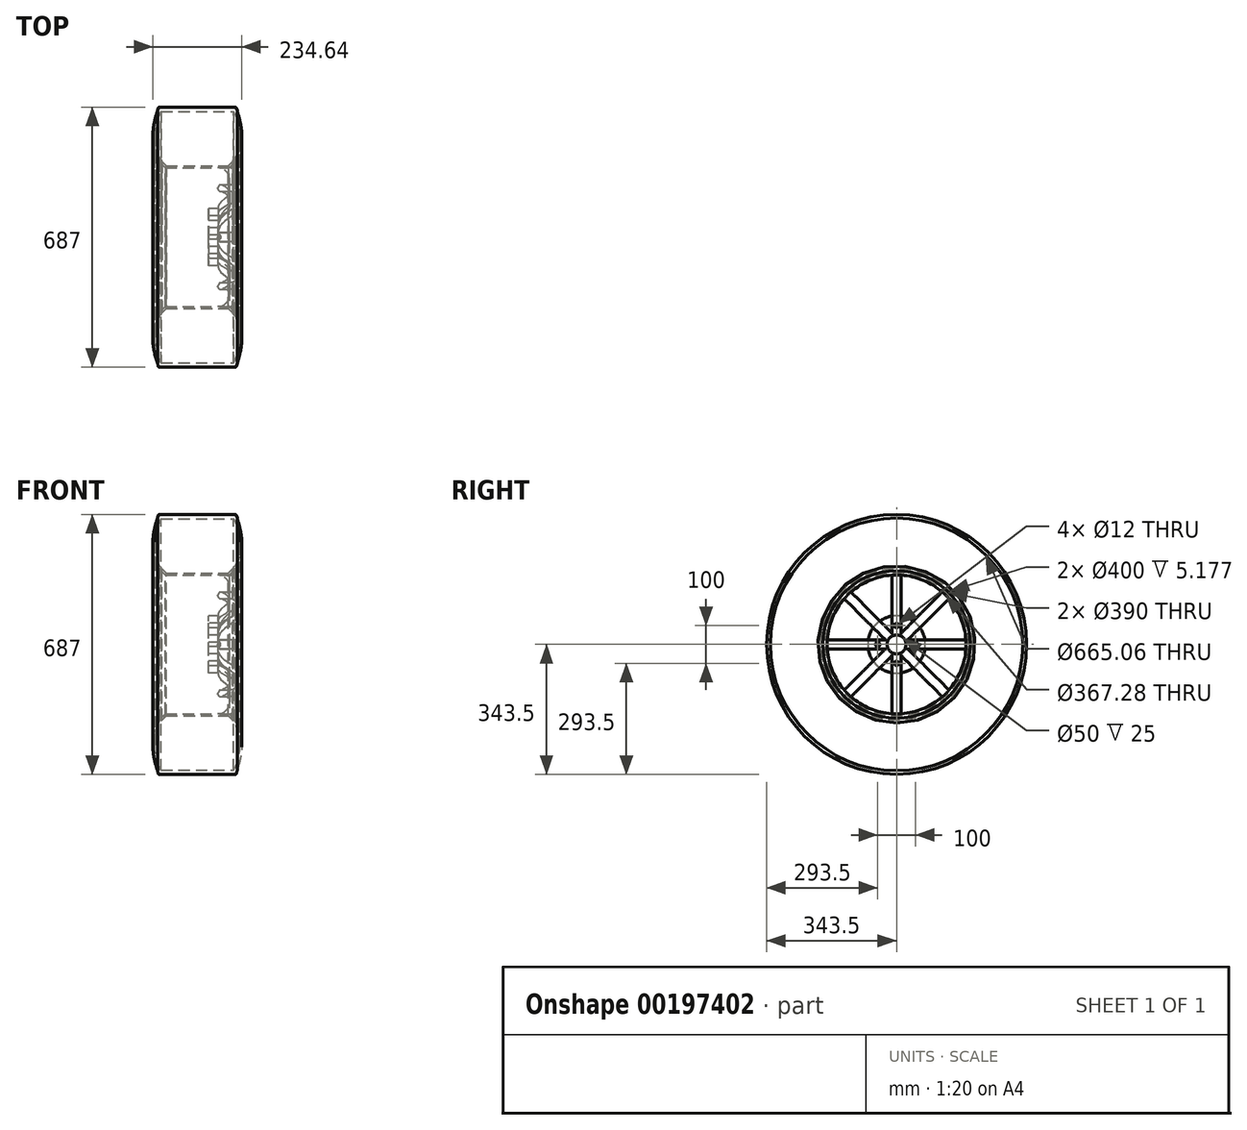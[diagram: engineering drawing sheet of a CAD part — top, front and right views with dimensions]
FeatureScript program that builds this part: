
annotation { "Feature Type Name" : "Feature", "Feature Type Description" : "" }
export const myFeature = defineFeature(function(context is Context, id is Id, definition is map)
    precondition{}
    {
        {
            var Q0;
            Q0=qCreatedBy(makeId("Front.planeOp"),FACE);
            var sketch = newSketch(context, id + "F0", { "sketchPlane" : qUnion([Q0])});
            skLineSegment(sketch, "E0", {"start": v(-136.6, 197.98) * mm, "end": v(-136.6, 205) * mm});
            skLineSegment(sketch, "E1", {"start": v(-131.6, 205) * mm, "end": v(-131.6, 202) * mm});
            skLineSegment(sketch, "E2", {"start": v(-129.6, 200) * mm, "end": v(-123.6, 200) * mm});
            skLineSegment(sketch, "E3", {"start": v(63.6, 200) * mm, "end": v(69.6, 200) * mm});
            skLineSegment(sketch, "E4", {"start": v(71.6, 202) * mm, "end": v(71.6, 205) * mm});
            skLineSegment(sketch, "E5", {"start": v(76.6, 205) * mm, "end": v(76.6, 195.82) * mm});
            skArc(sketch, "E6", {"start": v(-131.6, 205) * mm, "mid": v(-134.1, 207.5) * mm, "end": v(-136.6, 205) * mm});
            skArc(sketch, "E7", {"start": v(76.6, 205) * mm, "mid": v(74.1, 207.5) * mm, "end": v(71.6, 205) * mm});
            skLineSegment(sketch, "E8", {"start": v(0, 0) * mm, "end": v(-237.92, 0) * mm, "construction": true});
            skPoint(sketch, "E9.visualSharp", {"position": v(-136.6, 195) * mm});
            skArc(sketch, "E9.filletArc", {"start": v(-136.6, 197.98) * mm, "mid": v(-135.84, 195.98) * mm, "end": v(-133.93, 195) * mm});
            skPoint(sketch, "E10.visualSharp", {"position": v(-131.6, 200) * mm});
            skArc(sketch, "E10.filletArc", {"start": v(-131.6, 202) * mm, "mid": v(-131.01, 200.59) * mm, "end": v(-129.6, 200) * mm});
            skPoint(sketch, "E11.visualSharp", {"position": v(76.6, 195) * mm});
            skArc(sketch, "E11.filletArc", {"start": v(76.49, 195) * mm, "mid": v(76.57, 195.4) * mm, "end": v(76.6, 195.82) * mm});
            skPoint(sketch, "E12.visualSharp", {"position": v(71.6, 200) * mm});
            skArc(sketch, "E12.filletArc", {"start": v(69.6, 200) * mm, "mid": v(71.01, 200.59) * mm, "end": v(71.6, 202) * mm});
            skLineSegment(sketch, "E13", {"start": v(0, 0) * mm, "end": v(0, 286.07) * mm, "construction": true});
            skLineSegment(sketch, "E14", {"start": v(-30, 283.92) * mm, "end": v(-30, -44.36) * mm, "construction": true});
            skLineSegment(sketch, "E15", {"start": v(-123.6, 200) * mm, "end": v(-112.24, 188.64) * mm});
            skLineSegment(sketch, "E16", {"start": v(-112.24, 188.64) * mm, "end": v(52.24, 188.64) * mm});
            skLineSegment(sketch, "E17", {"start": v(52.24, 188.64) * mm, "end": v(63.6, 200) * mm});
            skLineSegment(sketch, "E18", {"start": v(-133.93, 195) * mm, "end": v(-125.67, 195) * mm});
            skLineSegment(sketch, "E19", {"start": v(-125.67, 195) * mm, "end": v(-114.3, 183.64) * mm});
            skLineSegment(sketch, "E20", {"start": v(-114.3, 183.64) * mm, "end": v(54.3, 183.64) * mm});
            skLineSegment(sketch, "E21", {"start": v(54.3, 183.64) * mm, "end": v(65.67, 195) * mm});
            skLineSegment(sketch, "E22", {"start": v(65.67, 195) * mm, "end": v(76.49, 195) * mm});
            skSolve(sketch);
        }
        {
            var Q0;
            Q0 = qSketchRegion(id + "F0", true);
            var Q1;
            Q1=sQuery(id+"F0.wireOp",EDGE,"E8");
            revolve(context, id + "F1", {"entities" : qUnion([Q0]), "axis" : qUnion([Q1]), "revolveType" : RevolveType.FULL});
        }
        {
            var Q0;
            Q0=qCreatedBy(makeId("Right.planeOp"),FACE);
            var sketch = newSketch(context, id + "F2", { "sketchPlane" : qUnion([Q0])});
            skCircle(sketch, "E23", {"center": v(0, 0) * mm, "radius": 76 * mm});
            skCircle(sketch, "E24", {"center": v(0, 0) * mm, "radius": 25 * mm});
            skSolve(sketch);
        }
        {
            var Q0;
            Q0 = qSketchRegion(id + "F2", true);
            extrude(context, id + "F3", {"entities" : qUnion([Q0]), "depth" : 25 * mm});
        }
        {
            var Q0;
            Q0=qCreatedBy(makeId("Front.planeOp"),FACE);
            var sketch = newSketch(context, id + "F4", { "sketchPlane" : qUnion([Q0])});
            skLineSegment(sketch, "E25", {"start": v(72.7, 165.26) * mm, "end": v(72.7, 117.72) * mm});
            skLineSegment(sketch, "E26", {"start": v(61.14, 89.83) * mm, "end": v(43.45, 72.14) * mm});
            skLineSegment(sketch, "E27.0", {"start": v(-114.3, 183.64) * mm, "end": v(54.3, 183.64) * mm, "construction": true});
            skLineSegment(sketch, "E28.0", {"start": v(25, 76) * mm, "end": v(25, -76) * mm, "construction": true});
            skArc(sketch, "E29", {"start": v(72.7, 165.26) * mm, "mid": v(67.3, 178.25) * mm, "end": v(54.3, 183.64) * mm});
            skArc(sketch, "E30", {"start": v(61.14, 89.83) * mm, "mid": v(69.69, 102.63) * mm, "end": v(72.7, 117.72) * mm});
            skArc(sketch, "E31", {"start": v(43.45, 72.14) * mm, "mid": v(29.8, 51.7) * mm, "end": v(25, 27.6) * mm});
            skLineSegment(sketch, "E32", {"start": v(32.13, 91.93) * mm, "end": v(45.77, 104.12) * mm});
            skLineSegment(sketch, "E33", {"start": v(55.4, 125.61) * mm, "end": v(55.4, 151.99) * mm});
            skArc(sketch, "E34", {"start": v(32.13, 91.93) * mm, "mid": v(26.86, 84.72) * mm, "end": v(25, 76) * mm});
            skArc(sketch, "E35", {"start": v(45.77, 104.12) * mm, "mid": v(52.88, 113.84) * mm, "end": v(55.4, 125.61) * mm});
            skArc(sketch, "E36", {"start": v(55.4, 151.99) * mm, "mid": v(46.12, 174.37) * mm, "end": v(23.74, 183.64) * mm});
            skLineSegment(sketch, "E37", {"start": v(23.74, 183.64) * mm, "end": v(54.3, 183.64) * mm});
            skLineSegment(sketch, "E38", {"start": v(25, 76) * mm, "end": v(25, 27.6) * mm});
            skSolve(sketch);
        }
        {
            var Q0;
            Q0 = qSketchRegion(id + "F4", true);
            extrude(context, id + "F5", {"entities" : qUnion([Q0]), "endBound" : BoundingType.SYMMETRIC, "depth" : 25 * mm});
        }
        {
            var Q0;
            Q0=makeQuery(id+"F5.opExtrude","SWEPT_BODY",BODY,{"disambiguationData":[OSD([sQuery(id+"F4.wireOp",EDGE,"E25"),sQuery(id+"F4.wireOp",EDGE,"E26"),sQuery(id+"F4.wireOp",EDGE,"E29"),sQuery(id+"F4.wireOp",EDGE,"E30"),sQuery(id+"F4.wireOp",EDGE,"E31"),sQuery(id+"F4.wireOp",EDGE,"E32"),sQuery(id+"F4.wireOp",EDGE,"E33"),sQuery(id+"F4.wireOp",EDGE,"E34"),sQuery(id+"F4.wireOp",EDGE,"E35"),sQuery(id+"F4.wireOp",EDGE,"E36"),sQuery(id+"F4.wireOp",EDGE,"E37"),sQuery(id+"F4.wireOp",EDGE,"E38")])]});
            var Q1;
            Q1=makeQuery(id+"F3.opExtrude","CAP_EDGE",EDGE,{"disambiguationData":[OSD([sQuery(id+"F2.wireOp",EDGE,"E24")])],"isStart":false});
            circularPattern(context, id + "F6", {"operationType" : NewBodyOperationType.ADD, "entities" : qUnion([Q0]), "axis" : qUnion([Q1]), "angle" : 360 * degree, "instanceCount" : 8, "equalSpace" : true});
        }
        {
            var Q0;
            Q0=qCreatedBy(makeId("Right.planeOp"),FACE);
            var sketch = newSketch(context, id + "F7", { "sketchPlane" : qUnion([Q0])});
            skCircle(sketch, "E39", {"center": v(0, 50) * mm, "radius": 6 * mm});
            skCircle(sketch, "E40.1.0", {"center": v(-50, 0) * mm, "radius": 6 * mm});
            skCircle(sketch, "E40.2.0", {"center": v(0, -50) * mm, "radius": 6 * mm});
            skCircle(sketch, "E40.3.0", {"center": v(50, 0) * mm, "radius": 6 * mm});
            skPoint(sketch, "E40.center", {"position": v(0, 0) * mm});
            skSolve(sketch);
        }
        {
            var Q0;
            Q0 = qSketchRegion(id + "F7", true);
            extrude(context, id + "F8", {"entities" : qUnion([Q0]), "operationType" : NewBodyOperationType.REMOVE, "endBound" : BoundingType.THROUGH_ALL, "depth" : 25 * mm});
        }
        {
            var Q0;
            Q0=qCreatedBy(makeId("Front.planeOp"),FACE);
            var sketch = newSketch(context, id + "F9", { "sketchPlane" : qUnion([Q0])});
            skLineSegment(sketch, "E41", {"start": v(-130.28, 343.5) * mm, "end": v(72.5, 343.5) * mm});
            skLineSegment(sketch, "E42", {"start": v(-131.6, 205) * mm, "end": v(-131.6, 202) * mm});
            skLineSegment(sketch, "E43", {"start": v(-129.6, 200) * mm, "end": v(-124.42, 200) * mm});
            skLineSegment(sketch, "E44", {"start": v(-124.42, 200) * mm, "end": v(-124.42, 203.1) * mm});
            skPoint(sketch, "E45.visualSharp", {"position": v(-131.6, 200) * mm});
            skArc(sketch, "E45.filletArc", {"start": v(-131.6, 202) * mm, "mid": v(-131.01, 200.59) * mm, "end": v(-129.6, 200) * mm});
            skLineSegment(sketch, "E46.0", {"start": v(-131.6, 205) * mm, "end": v(-131.6, -205) * mm, "construction": true});
            skLineSegment(sketch, "E47", {"start": v(-129.6, 200) * mm, "end": v(-123.6, 200) * mm, "construction": true});
            skLineSegment(sketch, "E48", {"start": v(-30, 342.1) * mm, "end": v(-30, 134.1) * mm, "construction": true});
            skLineSegment(sketch, "E49.0", {"start": v(71.6, 205) * mm, "end": v(71.6, -205) * mm, "construction": true});
            skLineSegment(sketch, "E50", {"start": v(-133.15, 341.38) * mm, "end": v(-135.42, 333.94) * mm});
            skPoint(sketch, "E51.visualSharp", {"position": v(-132.5, 343.5) * mm});
            skArc(sketch, "E51.filletArc", {"start": v(-130.28, 343.5) * mm, "mid": v(-132.06, 342.91) * mm, "end": v(-133.15, 341.38) * mm});
            skLineSegment(sketch, "E52", {"start": v(-30, 332.53) * mm, "end": v(-125.81, 332.53) * mm});
            skFitSpline(sketch, "E53", {"points": [v(-131.6, 205) * mm, v(-134.64, 210.68) * mm, v(-147.14, 264.8) * mm, v(-135.42, 333.94) * mm], "startDerivative": vector(-18.9, 28.85) * mm, "endDerivative": vector(43.05, 146.95) * mm});
            skFitSpline(sketch, "E54", {"points": [v(-125.81, 332.53) * mm, v(-140.64, 292.05) * mm, v(-140.04, 244) * mm, v(-130.56, 208.88) * mm, v(-128.1, 205.94) * mm, v(-124.42, 203.1) * mm], "startDerivative": vector(-81.6, -139.7) * mm, "endDerivative": vector(2.35, -25.42) * mm});
            skArc(sketch, "E55.MirrorCS", {"start": v(70.28, 343.5) * mm, "mid": v(72.06, 342.91) * mm, "end": v(73.15, 341.38) * mm});
            skLineSegment(sketch, "E56.MirrorCS", {"start": v(73.15, 341.38) * mm, "end": v(75.42, 333.94) * mm});
            skPoint(sketch, "E57.MirrorP", {"position": v(72.5, 343.5) * mm});
            skFitSpline(sketch, "E58.MirrorCS", {"points": [v(71.6, 205) * mm, v(74.64, 210.68) * mm, v(87.14, 264.8) * mm, v(75.42, 333.94) * mm], "startDerivative": vector(18.9, 28.85) * mm, "endDerivative": vector(-43.05, 146.95) * mm});
            skFitSpline(sketch, "E59.MirrorCS", {"points": [v(65.81, 332.53) * mm, v(80.64, 292.05) * mm, v(80.04, 244) * mm, v(70.56, 208.88) * mm, v(68.1, 205.94) * mm, v(64.42, 203.1) * mm], "startDerivative": vector(81.6, -139.7) * mm, "endDerivative": vector(-2.35, -25.42) * mm});
            skLineSegment(sketch, "E60.MirrorCS", {"start": v(-30, 332.53) * mm, "end": v(65.81, 332.53) * mm});
            skArc(sketch, "E61.MirrorCS", {"start": v(71.6, 202) * mm, "mid": v(71.01, 200.59) * mm, "end": v(69.6, 200) * mm});
            skLineSegment(sketch, "E62.MirrorCS", {"start": v(69.6, 200) * mm, "end": v(64.42, 200) * mm});
            skLineSegment(sketch, "E63.MirrorCS", {"start": v(69.6, 200) * mm, "end": v(63.6, 200) * mm, "construction": true});
            skLineSegment(sketch, "E64.MirrorCS", {"start": v(71.6, 205) * mm, "end": v(71.6, 202) * mm});
            skPoint(sketch, "E65.MirrorP", {"position": v(71.6, 200) * mm});
            skLineSegment(sketch, "E66.MirrorCS", {"start": v(64.42, 200) * mm, "end": v(64.42, 203.1) * mm});
            skLineSegment(sketch, "E67", {"start": v(0, 0) * mm, "end": v(-276.68, 0) * mm, "construction": true});
            skSolve(sketch);
        }
        {
            var Q0;
            Q0 = qSketchRegion(id + "F9", true);
            var Q1;
            Q1=sQuery(id+"F9.wireOp",EDGE,"E67");
            revolve(context, id + "F10", {"entities" : qUnion([Q0]), "axis" : qUnion([Q1]), "revolveType" : RevolveType.FULL});
        }
    });
